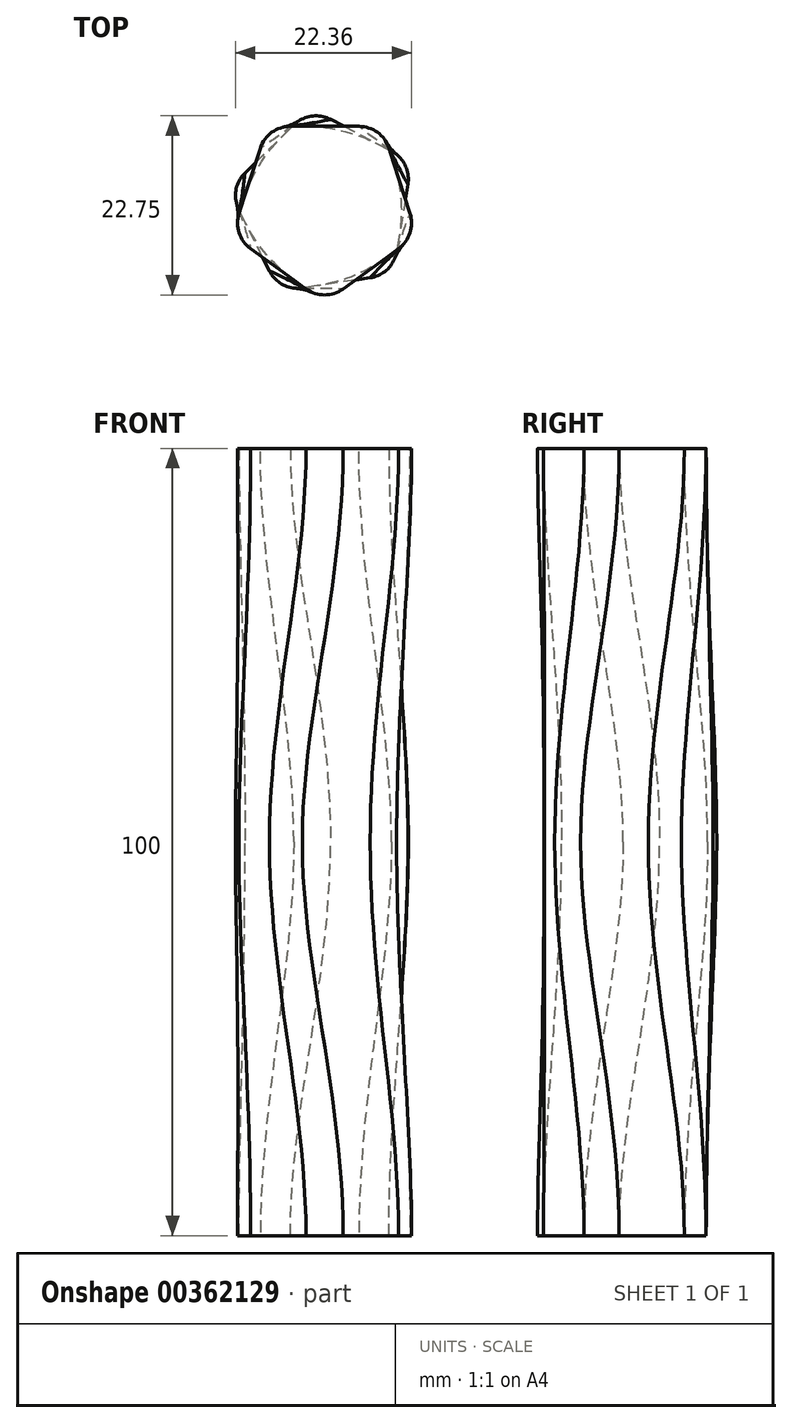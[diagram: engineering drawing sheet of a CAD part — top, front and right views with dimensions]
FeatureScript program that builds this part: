
annotation { "Feature Type Name" : "Feature", "Feature Type Description" : "" }
export const myFeature = defineFeature(function(context is Context, id is Id, definition is map)
    precondition{}
    {
        {
            var Q0;
            Q0=qCreatedBy(makeId("Top.planeOp"),FACE);
            cPlane(context, id + "F0", {"entities" : qUnion([Q0]), "cplaneType" : CPlaneType.OFFSET, "offset" : 50 * mm, "width" : 150 * mm, "height" : 150 * mm});
        }
        {
            var Q0;
            Q0=qCreatedBy(makeId("Top.planeOp"),FACE);
            var sketch = newSketch(context, id + "F1", { "sketchPlane" : qUnion([Q0])});
            skCircle(sketch, "E0.cCircle", {"center": v(0, 0) * mm, "radius": 10 * mm, "construction": true});
            skLineSegment(sketch, "E0.0", {"start": v(-7.27, 10) * mm, "end": v(7.27, 10) * mm});
            skLineSegment(sketch, "E0.1", {"start": v(7.27, 10) * mm, "end": v(11.76, -3.82) * mm});
            skLineSegment(sketch, "E0.2", {"start": v(11.76, -3.82) * mm, "end": v(0, -12.36) * mm});
            skLineSegment(sketch, "E0.3", {"start": v(0, -12.36) * mm, "end": v(-11.76, -3.82) * mm});
            skLineSegment(sketch, "E0.4", {"start": v(-11.76, -3.82) * mm, "end": v(-7.27, 10) * mm});
            skPoint(sketch, "E0.0.midPoint", {"position": v(0, 10) * mm});
            skSolve(sketch);
        }
        {
            var Q0;
            Q0=qCreatedBy(id+"F0.planeOp",FACE);
            var sketch = newSketch(context, id + "F2", { "sketchPlane" : qUnion([Q0])});
            skCircle(sketch, "E1.cCircle", {"center": v(0, 0) * mm, "radius": 10 * mm, "construction": true});
            skLineSegment(sketch, "E1.0", {"start": v(11.06, 5.52) * mm, "end": v(8.66, -8.82) * mm});
            skLineSegment(sketch, "E1.1", {"start": v(8.66, -8.82) * mm, "end": v(-5.7, -10.96) * mm});
            skLineSegment(sketch, "E1.2", {"start": v(-5.7, -10.96) * mm, "end": v(-12.2, 2.04) * mm});
            skLineSegment(sketch, "E1.3", {"start": v(-12.2, 2.04) * mm, "end": v(-1.83, 12.22) * mm});
            skLineSegment(sketch, "E1.4", {"start": v(-1.83, 12.22) * mm, "end": v(11.06, 5.52) * mm});
            skPoint(sketch, "E1.0.midPoint", {"position": v(10, 0) * mm});
            skSolve(sketch);
        }
        {
            var Q0;
            Q0=makeQuery(id+"F1.imprint","IMPRINT",FACE,{"disambiguationData":[TD([[makeQuery(id+"F1.imprint","IMPRINT",EDGE,{"derivedFrom":sQuery(id+"F1.wireOp",EDGE,"E0.0")}),-1.0]])]});
            var Q1;
            Q1=makeQuery(id+"F2.imprint","IMPRINT",FACE,{"disambiguationData":[TD([[makeQuery(id+"F2.imprint","IMPRINT",EDGE,{"derivedFrom":sQuery(id+"F2.wireOp",EDGE,"E1.0")}),-1.0]])]});
            loft(context, id + "F3", {"startCondition" : LoftEndDerivativeType.NORMAL_TO_PROFILE, "startMagnitude" : 1, "endCondition" : LoftEndDerivativeType.NORMAL_TO_PROFILE, "endMagnitude" : 1, "sheetProfilesArray" : [{ "sheetProfileEntities" : qUnion([Q0]) }, { "sheetProfileEntities" : qUnion([Q1]) }]});
        }
        {
            var Q0;
            Q0=makeQuery(id+"F3.opLoft","SWEPT_EDGE",EDGE,{"disambiguationData":[OSD([sQuery(id+"F1.wireOp",EDGE,"E0.3"),sQuery(id+"F1.wireOp",EDGE,"E0.4"),sQuery(id+"F2.wireOp",EDGE,"E1.2"),sQuery(id+"F2.wireOp",EDGE,"E1.3")])]});
            var Q1;
            Q1=makeQuery(id+"F3.opLoft","SWEPT_EDGE",EDGE,{"disambiguationData":[OSD([sQuery(id+"F1.wireOp",EDGE,"E0.2"),sQuery(id+"F1.wireOp",EDGE,"E0.3"),sQuery(id+"F2.wireOp",EDGE,"E1.1"),sQuery(id+"F2.wireOp",EDGE,"E1.2")])]});
            var Q2;
            Q2=makeQuery(id+"F3.opLoft","SWEPT_EDGE",EDGE,{"disambiguationData":[OSD([sQuery(id+"F1.wireOp",EDGE,"E0.1"),sQuery(id+"F1.wireOp",EDGE,"E0.2"),sQuery(id+"F2.wireOp",EDGE,"E1.0"),sQuery(id+"F2.wireOp",EDGE,"E1.1")])]});
            var Q3;
            Q3=makeQuery(id+"F3.opLoft","SWEPT_EDGE",EDGE,{"disambiguationData":[OSD([sQuery(id+"F1.wireOp",EDGE,"E0.0"),sQuery(id+"F1.wireOp",EDGE,"E0.1"),sQuery(id+"F2.wireOp",EDGE,"E1.0"),sQuery(id+"F2.wireOp",EDGE,"E1.4")])]});
            var Q4;
            Q4=makeQuery(id+"F3.opLoft","SWEPT_EDGE",EDGE,{"disambiguationData":[OSD([sQuery(id+"F1.wireOp",EDGE,"E0.0"),sQuery(id+"F1.wireOp",EDGE,"E0.4"),sQuery(id+"F2.wireOp",EDGE,"E1.3"),sQuery(id+"F2.wireOp",EDGE,"E1.4")])]});
            fillet(context, id + "F4", {"entities" : qUnion([Q0, Q1, Q2, Q3, Q4]), "radius" : 4 * mm, "tangentPropagation" : true, "allowEdgeOverflow" : false});
        }
        {
            var Q0;
            Q0=makeQuery(id+"F3.opLoft","SWEPT_BODY",BODY,{"disambiguationData":[OSD([makeQuery(id+"F1.imprint","IMPRINT",FACE,{"disambiguationData":[TD([[makeQuery(id+"F1.imprint","IMPRINT",EDGE,{"derivedFrom":sQuery(id+"F1.wireOp",EDGE,"E0.0")}),-1.0]])]}),makeQuery(id+"F2.imprint","IMPRINT",FACE,{"disambiguationData":[TD([[makeQuery(id+"F2.imprint","IMPRINT",EDGE,{"derivedFrom":sQuery(id+"F2.wireOp",EDGE,"E1.0")}),-1.0]])]})])]});
            var Q1;
            Q1=makeQuery(id+"F3.opLoft","CAP_FACE",FACE,{"disambiguationData":[OSD([makeQuery(id+"F2.imprint","IMPRINT",FACE,{"disambiguationData":[TD([[makeQuery(id+"F2.imprint","IMPRINT",EDGE,{"derivedFrom":sQuery(id+"F2.wireOp",EDGE,"E1.0")}),-1.0]])]})])],"isStart":true});
            mirror(context, id + "F5", {"operationType" : NewBodyOperationType.ADD, "entities" : qUnion([Q0]), "mirrorPlane" : qUnion([Q1])});
        }
    });
